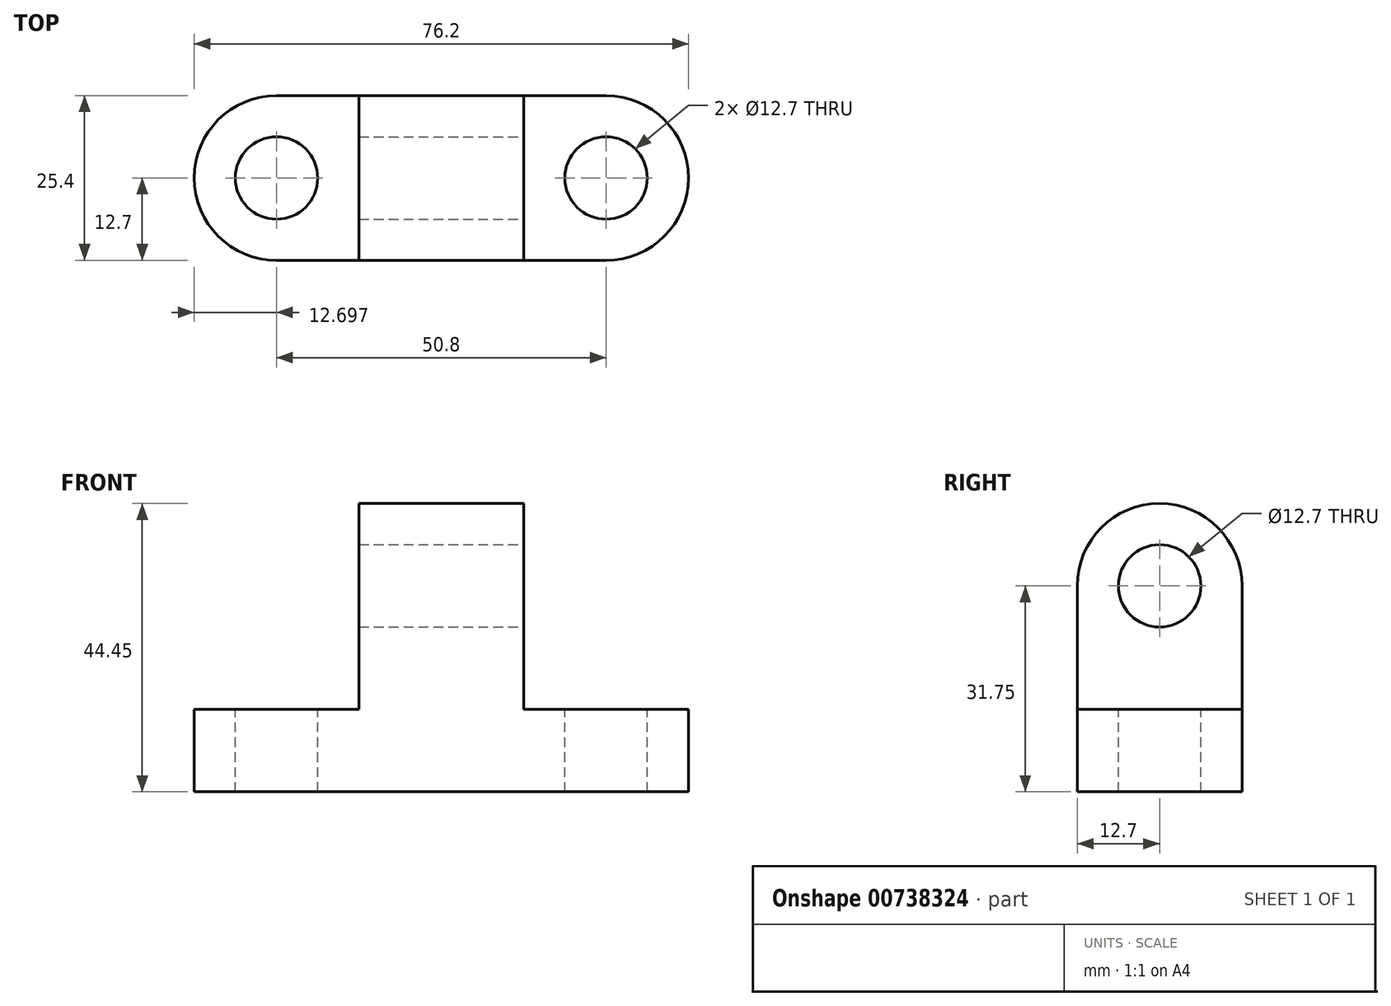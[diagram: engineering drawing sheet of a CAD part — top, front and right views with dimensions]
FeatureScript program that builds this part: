
annotation { "Feature Type Name" : "Feature", "Feature Type Description" : "" }
export const myFeature = defineFeature(function(context is Context, id is Id, definition is map)
    precondition{}
    {
        {
            var Q0;
            Q0=qCreatedBy(makeId("Front.planeOp"),FACE);
            var sketch = newSketch(context, id + "F0", { "sketchPlane" : qUnion([Q0])});
            skLineSegment(sketch, "E0", {"start": v(-31.27, 0) * mm, "end": v(-31.27, 12.7) * mm});
            skLineSegment(sketch, "E1", {"start": v(-31.27, 12.7) * mm, "end": v(-5.87, 12.7) * mm});
            skLineSegment(sketch, "E2", {"start": v(-5.87, 12.7) * mm, "end": v(-5.87, 44.45) * mm});
            skLineSegment(sketch, "E3", {"start": v(-5.87, 44.45) * mm, "end": v(19.53, 44.45) * mm});
            skLineSegment(sketch, "E4", {"start": v(19.53, 44.45) * mm, "end": v(19.53, 12.7) * mm});
            skLineSegment(sketch, "E5", {"start": v(19.53, 12.7) * mm, "end": v(44.93, 12.7) * mm});
            skLineSegment(sketch, "E6", {"start": v(44.93, 12.7) * mm, "end": v(44.93, 0) * mm});
            skLineSegment(sketch, "E7", {"start": v(44.93, 0) * mm, "end": v(-31.27, 0) * mm});
            skSolve(sketch);
        }
        {
            var Q0;
            Q0=makeQuery(id+"F0.imprint","IMPRINT",FACE,{"disambiguationData":[TD([[makeQuery(id+"F0.imprint","IMPRINT",EDGE,{"derivedFrom":sQuery(id+"F0.wireOp",EDGE,"E0")}),-1.0]])]});
            extrude(context, id + "F1", {"entities" : qUnion([Q0]), "depth" : 25.4 * mm, "offsetDistance" : 25.4 * mm});
        }
        {
            var Q0;
            Q0=makeQuery(id+"F1.opExtrude","SWEPT_FACE",FACE,{"disambiguationData":[OSD([sQuery(id+"F0.wireOp",EDGE,"E5")])]});
            var sketch = newSketch(context, id + "F2", { "sketchPlane" : qUnion([Q0])});
            skLineSegment(sketch, "E8", {"start": v(32.23, 0) * mm, "end": v(32.23, -25.4) * mm});
            skLineSegment(sketch, "E9", {"start": v(44.93, -25.4) * mm, "end": v(32.23, -25.4) * mm});
            skCircle(sketch, "E10", {"center": v(32.23, -12.7) * mm, "radius": 6.35 * mm});
            skArc(sketch, "E11", {"start": v(32.23, -25.4) * mm, "mid": v(44.93, -12.7) * mm, "end": v(32.23, 0) * mm});
            skSolve(sketch);
        }
        {
            var Q0;
            {var subQ0=sQuery(id+"F2.wireOp",EDGE,"E10");var subQ1=sQuery(id+"F2.wireOp",EDGE,"E8");var subQ2=makeQuery(id+"F2.imprint","INTERSECT",VERTEX,{"disambiguationData":[OD(0.0)],"derivedFrom":[subQ1,subQ0]});Q0=makeQuery(id+"F2.imprint","IMPRINT",FACE,{"disambiguationData":[TD([[makeQuery(id+"F2.imprint","IMPRINT",EDGE,{"disambiguationData":[TD([[subQ2,-1.0]])],"derivedFrom":subQ1}),1.0]])]});}
            var Q1;
            {var subQ0=sQuery(id+"F2.wireOp",EDGE,"E10");var subQ1=sQuery(id+"F2.wireOp",EDGE,"E8");var subQ2=makeQuery(id+"F2.imprint","INTERSECT",VERTEX,{"disambiguationData":[OD(0.0)],"derivedFrom":[subQ1,subQ0]});Q1=makeQuery(id+"F2.imprint","IMPRINT",FACE,{"disambiguationData":[TD([[makeQuery(id+"F2.imprint","IMPRINT",EDGE,{"disambiguationData":[TD([[subQ2,-1.0]])],"derivedFrom":subQ1}),-1.0]])]});}
            var Q2;
            {var subQ0=sQuery(id+"F2.wireOp",EDGE,"E11");var subQ1=sQuery(id+"F0.wireOp",EDGE,"E5");var subQ2=makeQuery(id+"F1.opExtrude","CAP_EDGE",EDGE,{"disambiguationData":[OSD([subQ1])],"isStart":true});var subQ3=makeQuery(id+"F2.imprint","INTERSECT",VERTEX,{"derivedFrom":[subQ2,sQuery(id+"F2.wireOp",EDGE,"E8"),subQ0]});Q2=makeQuery(id+"F2.imprint","IMPRINT",FACE,{"disambiguationData":[TD([[makeQuery(id+"F2.imprint","IMPRINT",EDGE,{"disambiguationData":[TD([[subQ3,1.0]])],"derivedFrom":subQ0}),-1.0]])]});}
            var Q3;
            {var subQ0=sQuery(id+"F2.wireOp",EDGE,"E9");Q3=makeQuery(id+"F2.imprint","IMPRINT",FACE,{"disambiguationData":[TD([[makeQuery(id+"F2.imprint","IMPRINT",EDGE,{"derivedFrom":subQ0}),1.0]])]});}
            extrude(context, id + "F3", {"entities" : qUnion([Q0, Q1, Q2, Q3]), "operationType" : NewBodyOperationType.REMOVE, "endBound" : BoundingType.THROUGH_ALL, "oppositeDirection" : true, "depth" : 25.4 * mm, "offsetDistance" : 25.4 * mm});
        }
        {
            var Q0;
            Q0=makeQuery(id+"F1.opExtrude","SWEPT_FACE",FACE,{"disambiguationData":[OSD([sQuery(id+"F0.wireOp",EDGE,"E1")])]});
            var sketch = newSketch(context, id + "F4", { "sketchPlane" : qUnion([Q0])});
            skLineSegment(sketch, "E12", {"start": v(-18.57, 0) * mm, "end": v(-18.57, -25.4) * mm});
            skLineSegment(sketch, "E13", {"start": v(-18.57, -25.4) * mm, "end": v(-31.27, -25.4) * mm});
            skCircle(sketch, "E14", {"center": v(-18.57, -12.7) * mm, "radius": 6.35 * mm});
            skArc(sketch, "E15", {"start": v(-18.57, 0) * mm, "mid": v(-31.27, -12.7) * mm, "end": v(-18.57, -25.4) * mm});
            skSolve(sketch);
        }
        {
            var Q0;
            {var subQ0=sQuery(id+"F4.wireOp",EDGE,"E14");var subQ1=sQuery(id+"F4.wireOp",EDGE,"E12");var subQ2=makeQuery(id+"F4.imprint","INTERSECT",VERTEX,{"disambiguationData":[OD(0.0)],"derivedFrom":[subQ1,subQ0]});Q0=makeQuery(id+"F4.imprint","IMPRINT",FACE,{"disambiguationData":[TD([[makeQuery(id+"F4.imprint","IMPRINT",EDGE,{"disambiguationData":[TD([[subQ2,-1.0]])],"derivedFrom":subQ1}),1.0]])]});}
            var Q1;
            {var subQ0=sQuery(id+"F4.wireOp",EDGE,"E14");var subQ1=sQuery(id+"F4.wireOp",EDGE,"E12");var subQ2=makeQuery(id+"F4.imprint","INTERSECT",VERTEX,{"disambiguationData":[OD(0.0)],"derivedFrom":[subQ1,subQ0]});Q1=makeQuery(id+"F4.imprint","IMPRINT",FACE,{"disambiguationData":[TD([[makeQuery(id+"F4.imprint","IMPRINT",EDGE,{"disambiguationData":[TD([[subQ2,-1.0]])],"derivedFrom":subQ1}),-1.0]])]});}
            var Q2;
            {var subQ0=sQuery(id+"F4.wireOp",EDGE,"E15");var subQ1=sQuery(id+"F0.wireOp",EDGE,"E1");var subQ2=makeQuery(id+"F1.opExtrude","CAP_EDGE",EDGE,{"disambiguationData":[OSD([subQ1])],"isStart":true});var subQ3=makeQuery(id+"F4.imprint","INTERSECT",VERTEX,{"derivedFrom":[subQ2,sQuery(id+"F4.wireOp",EDGE,"E12"),subQ0]});Q2=makeQuery(id+"F4.imprint","IMPRINT",FACE,{"disambiguationData":[TD([[makeQuery(id+"F4.imprint","IMPRINT",EDGE,{"disambiguationData":[TD([[subQ3,-1.0]])],"derivedFrom":subQ0}),-1.0]])]});}
            var Q3;
            {var subQ0=sQuery(id+"F4.wireOp",EDGE,"E13");Q3=makeQuery(id+"F4.imprint","IMPRINT",FACE,{"disambiguationData":[TD([[makeQuery(id+"F4.imprint","IMPRINT",EDGE,{"derivedFrom":subQ0}),1.0]])]});}
            extrude(context, id + "F5", {"entities" : qUnion([Q0, Q1, Q2, Q3]), "operationType" : NewBodyOperationType.REMOVE, "endBound" : BoundingType.THROUGH_ALL, "oppositeDirection" : true, "depth" : 25.4 * mm, "offsetDistance" : 25.4 * mm});
        }
        {
            var Q0;
            Q0=makeQuery(id+"F1.opExtrude","SWEPT_FACE",FACE,{"disambiguationData":[OSD([sQuery(id+"F0.wireOp",EDGE,"E4")])]});
            var sketch = newSketch(context, id + "F6", { "sketchPlane" : qUnion([Q0])});
            skLineSegment(sketch, "E16", {"start": v(-25.4, 31.75) * mm, "end": v(0, 31.75) * mm});
            skLineSegment(sketch, "E17", {"start": v(0, 31.75) * mm, "end": v(0, 44.45) * mm});
            skCircle(sketch, "E18", {"center": v(-12.7, 31.75) * mm, "radius": 6.35 * mm});
            skArc(sketch, "E19", {"start": v(0, 31.75) * mm, "mid": v(-12.7, 44.45) * mm, "end": v(-25.4, 31.75) * mm});
            skSolve(sketch);
        }
        {
            var Q0;
            {var subQ0=sQuery(id+"F6.wireOp",EDGE,"E19");var subQ1=sQuery(id+"F0.wireOp",EDGE,"E4");var subQ2=makeQuery(id+"F1.opExtrude","CAP_EDGE",EDGE,{"disambiguationData":[OSD([subQ1])],"isStart":false});var subQ3=makeQuery(id+"F6.imprint","INTERSECT",VERTEX,{"derivedFrom":[subQ2,sQuery(id+"F6.wireOp",EDGE,"E16"),subQ0]});Q0=makeQuery(id+"F6.imprint","IMPRINT",FACE,{"disambiguationData":[TD([[makeQuery(id+"F6.imprint","IMPRINT",EDGE,{"disambiguationData":[TD([[subQ3,1.0]])],"derivedFrom":subQ0}),-1.0]])]});}
            var Q1;
            {var subQ0=sQuery(id+"F6.wireOp",EDGE,"E17");Q1=makeQuery(id+"F6.imprint","IMPRINT",FACE,{"disambiguationData":[TD([[makeQuery(id+"F6.imprint","IMPRINT",EDGE,{"derivedFrom":subQ0}),-1.0]])]});}
            var Q2;
            {var subQ0=sQuery(id+"F6.wireOp",EDGE,"E18");var subQ1=sQuery(id+"F6.wireOp",EDGE,"E16");var subQ2=makeQuery(id+"F6.imprint","INTERSECT",VERTEX,{"disambiguationData":[OD(0.0)],"derivedFrom":[subQ1,subQ0]});Q2=makeQuery(id+"F6.imprint","IMPRINT",FACE,{"disambiguationData":[TD([[makeQuery(id+"F6.imprint","IMPRINT",EDGE,{"disambiguationData":[TD([[subQ2,-1.0]])],"derivedFrom":subQ1}),1.0]])]});}
            var Q3;
            {var subQ0=sQuery(id+"F6.wireOp",EDGE,"E18");var subQ1=sQuery(id+"F6.wireOp",EDGE,"E16");var subQ2=makeQuery(id+"F6.imprint","INTERSECT",VERTEX,{"disambiguationData":[OD(0.0)],"derivedFrom":[subQ1,subQ0]});Q3=makeQuery(id+"F6.imprint","IMPRINT",FACE,{"disambiguationData":[TD([[makeQuery(id+"F6.imprint","IMPRINT",EDGE,{"disambiguationData":[TD([[subQ2,-1.0]])],"derivedFrom":subQ1}),-1.0]])]});}
            extrude(context, id + "F7", {"entities" : qUnion([Q0, Q1, Q2, Q3]), "operationType" : NewBodyOperationType.REMOVE, "endBound" : BoundingType.THROUGH_ALL, "oppositeDirection" : true, "depth" : 25.4 * mm, "offsetDistance" : 25.4 * mm});
        }
    });
